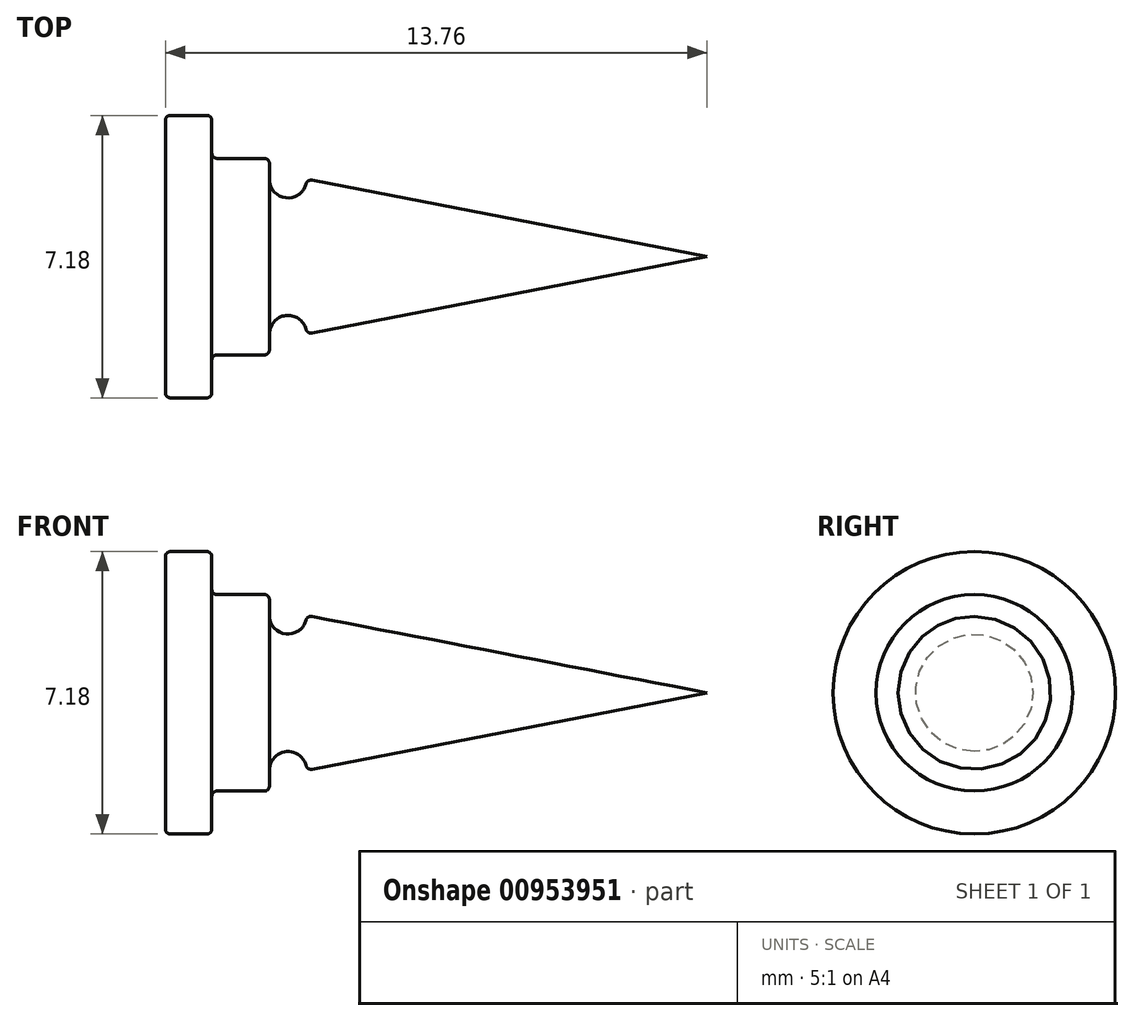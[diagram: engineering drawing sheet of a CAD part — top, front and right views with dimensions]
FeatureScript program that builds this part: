
annotation { "Feature Type Name" : "Feature", "Feature Type Description" : "" }
export const myFeature = defineFeature(function(context is Context, id is Id, definition is map)
    precondition{}
    {
        {
            var Q0;
            Q0=qCreatedBy(makeId("Top.planeOp"),FACE);
            var sketch = newSketch(context, id + "F0", { "sketchPlane" : qUnion([Q0])});
            skLineSegment(sketch, "E0", {"start": v(111.81, -6.83) * mm, "end": v(92.2, -6.83) * mm, "construction": true});
            skLineSegment(sketch, "E1", {"start": v(98.05, -3.24) * mm, "end": v(98.05, -6.83) * mm});
            skLineSegment(sketch, "E2", {"start": v(98.05, -3.24) * mm, "end": v(99.23, -3.24) * mm});
            skLineSegment(sketch, "E3", {"start": v(99.23, -3.24) * mm, "end": v(99.23, -4.33) * mm});
            skLineSegment(sketch, "E4", {"start": v(101.64, -4.86) * mm, "end": v(111.81, -6.83) * mm});
            skLineSegment(sketch, "E5", {"start": v(99.23, -4.33) * mm, "end": v(100.7, -4.33) * mm});
            skLineSegment(sketch, "E6", {"start": v(100.7, -4.33) * mm, "end": v(100.7, -4.86) * mm});
            skArc(sketch, "E7", {"start": v(100.7, -4.86) * mm, "mid": v(101.16, -5.34) * mm, "end": v(101.64, -4.86) * mm});
            skLineSegment(sketch, "E8", {"start": v(98.05, -6.83) * mm, "end": v(111.81, -6.83) * mm});
            skSolve(sketch);
        }
        {
            var Q0;
            Q0=makeQuery(id+"F0.imprint","IMPRINT",FACE,{"disambiguationData":[TD([[makeQuery(id+"F0.imprint","IMPRINT",EDGE,{"derivedFrom":sQuery(id+"F0.wireOp",EDGE,"E1")}),1.0]])]});
            var Q1;
            Q1=sQuery(id+"F0.wireOp",EDGE,"E0");
            revolve(context, id + "F1", {"surfaceOperationType" : NewSurfaceOperationType.NEW, "entities" : qUnion([Q0]), "axis" : qUnion([Q1]), "revolveType" : RevolveType.FULL});
        }
        {
            var Q0;
            Q0=makeQuery(id+"F1.opRevolve","SWEPT_FACE",FACE,{"disambiguationData":[OSD([sQuery(id+"F0.wireOp",EDGE,"E2")])]});
            var Q1;
            Q1=makeQuery(id+"F1.opRevolve","SWEPT_EDGE",EDGE,{"disambiguationData":[OSD([sQuery(id+"F0.wireOp",EDGE,"E5"),sQuery(id+"F0.wireOp",EDGE,"E6")])]});
            var Q2;
            Q2=makeQuery(id+"F1.opRevolve","SWEPT_EDGE",EDGE,{"disambiguationData":[OSD([sQuery(id+"F0.wireOp",EDGE,"E4"),sQuery(id+"F0.wireOp",EDGE,"E7")])]});
            var Q3;
            Q3=makeQuery(id+"F1.opRevolve","SWEPT_EDGE",EDGE,{"disambiguationData":[OSD([sQuery(id+"F0.wireOp",EDGE,"E3"),sQuery(id+"F0.wireOp",EDGE,"E5")])]});
            fillet(context, id + "F2", {"entities" : qUnion([Q0, Q1, Q2, Q3]), "radius" : 0.13 * mm, "tangentPropagation" : true, "allowEdgeOverflow" : false});
        }
    });
